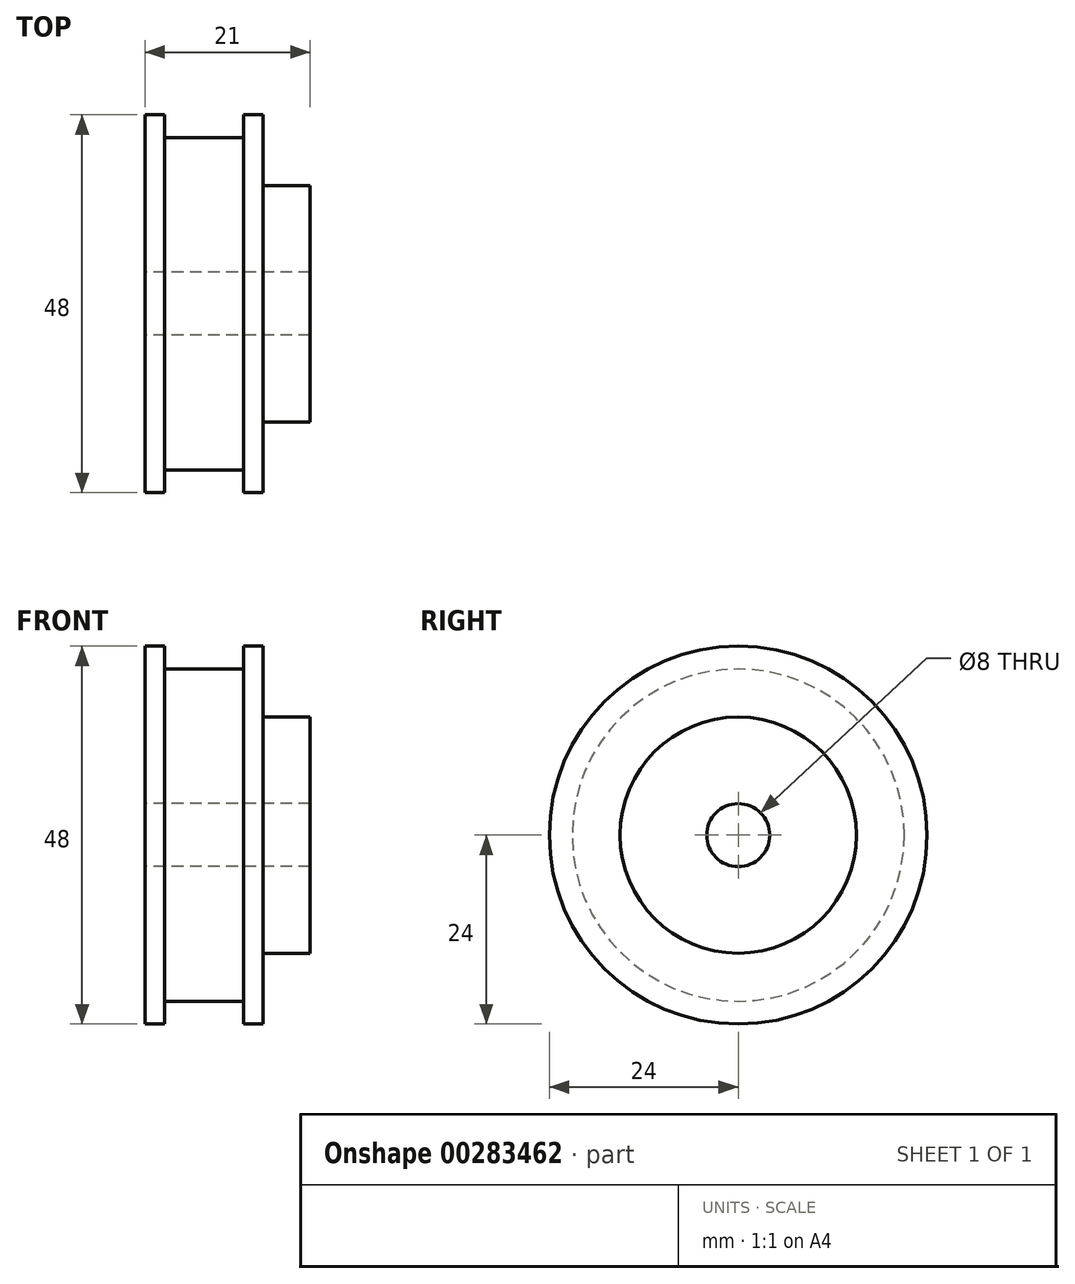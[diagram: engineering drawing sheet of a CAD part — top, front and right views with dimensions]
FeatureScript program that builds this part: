
annotation { "Feature Type Name" : "Feature", "Feature Type Description" : "" }
export const myFeature = defineFeature(function(context is Context, id is Id, definition is map)
    precondition{}
    {
        {
            var Q0;
            Q0=qCreatedBy(makeId("Front.planeOp"),FACE);
            var sketch = newSketch(context, id + "F0", { "sketchPlane" : qUnion([Q0])});
            skLineSegment(sketch, "E0", {"start": v(-18.22, 0) * mm, "end": v(20.5, 0) * mm, "construction": true});
            skLineSegment(sketch, "E1", {"start": v(6, 4) * mm, "end": v(-15, 4) * mm});
            skLineSegment(sketch, "E2", {"start": v(-15, 4) * mm, "end": v(-15, 24) * mm});
            skLineSegment(sketch, "E3", {"start": v(-15, 24) * mm, "end": v(-12.5, 24) * mm});
            skLineSegment(sketch, "E4", {"start": v(-12.5, 24) * mm, "end": v(-12.5, 21.1) * mm});
            skLineSegment(sketch, "E5", {"start": v(-12.5, 21.1) * mm, "end": v(-2.5, 21.1) * mm});
            skLineSegment(sketch, "E6", {"start": v(-2.5, 21.1) * mm, "end": v(-2.5, 24) * mm});
            skLineSegment(sketch, "E7", {"start": v(-2.5, 24) * mm, "end": v(0, 24) * mm});
            skLineSegment(sketch, "E8", {"start": v(0, 24) * mm, "end": v(0, 15) * mm});
            skLineSegment(sketch, "E9", {"start": v(0, 15) * mm, "end": v(6, 15) * mm});
            skLineSegment(sketch, "E10", {"start": v(6, 15) * mm, "end": v(6, 4) * mm});
            skSolve(sketch);
        }
        {
            var Q0;
            Q0=qSketchRegion(id+"F0",true);
            var Q1;
            Q1=sQuery(id+"F0.wireOp",EDGE,"E0");
            revolve(context, id + "F1", {"entities" : qUnion([Q0]), "axis" : qUnion([Q1]), "revolveType" : RevolveType.FULL});
        }
    });
